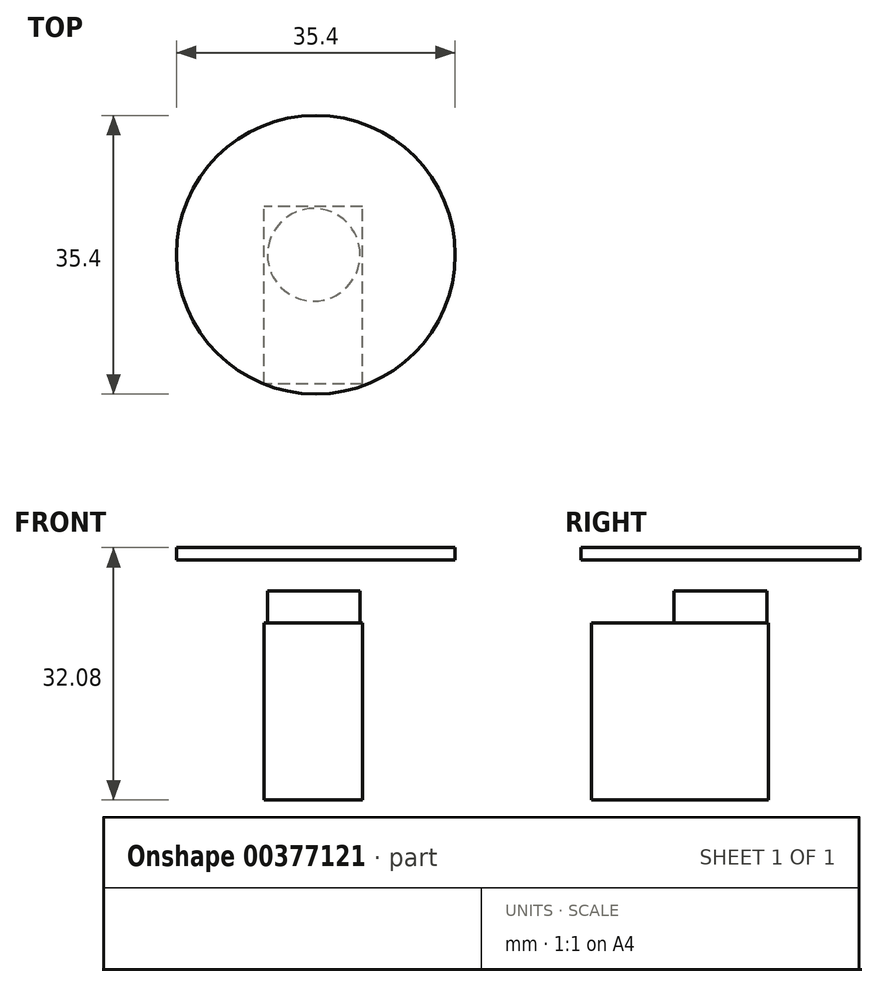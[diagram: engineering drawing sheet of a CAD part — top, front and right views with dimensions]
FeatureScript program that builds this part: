
annotation { "Feature Type Name" : "Feature", "Feature Type Description" : "" }
export const myFeature = defineFeature(function(context is Context, id is Id, definition is map)
    precondition{}
    {
        {
            var Q0;
            Q0=qCreatedBy(makeId("Right.planeOp"),FACE);
            var sketch = newSketch(context, id + "F0", { "sketchPlane" : qUnion([Q0])});
            skLineSegment(sketch, "E0.bottom", {"start": v(0, 0) * mm, "end": v(22.5, 0) * mm});
            skLineSegment(sketch, "E0.top", {"start": v(0, 22.5) * mm, "end": v(22.5, 22.5) * mm});
            skLineSegment(sketch, "E0.left", {"start": v(0, 0) * mm, "end": v(0, 22.5) * mm});
            skLineSegment(sketch, "E0.right", {"start": v(22.5, 0) * mm, "end": v(22.5, 22.5) * mm});
            skSolve(sketch);
        }
        {
            var Q0;
            Q0=makeQuery(id+"F0.imprint","IMPRINT",FACE,{"disambiguationData":[TD([[makeQuery(id+"F0.imprint","IMPRINT",EDGE,{"derivedFrom":sQuery(id+"F0.wireOp",EDGE,"E0.bottom")}),1.0]])]});
            extrude(context, id + "F1", {"entities" : qUnion([Q0]), "depth" : 12.5 * mm});
        }
        {
            var Q0;
            Q0=qCreatedBy(makeId("Top.planeOp"),FACE);
            var sketch = newSketch(context, id + "F2", { "sketchPlane" : qUnion([Q0])});
            skLineSegment(sketch, "E1", {"start": v(0, 0) * mm, "end": v(0, 12.4) * mm});
            skCircle(sketch, "E2", {"center": v(6.33, 16.4) * mm, "radius": 5.88 * mm});
            skSolve(sketch);
        }
        {
            var Q0;
            Q0 = qSketchRegion(id + "F2", true);
            extrude(context, id + "F3", {"entities" : qUnion([Q0]), "operationType" : NewBodyOperationType.ADD, "depth" : 26.6 * mm});
        }
        {
            var Q0;
            Q0=qCreatedBy(makeId("Top.planeOp"),FACE);
            var sketch = newSketch(context, id + "F4", { "sketchPlane" : qUnion([Q0])});
            skCircle(sketch, "E3", {"center": v(6.33, 16.55) * mm, "radius": 2.9 * mm});
            skSolve(sketch);
        }
        {
            var Q0;
            Q0=sQuery(id+"F4.wireOp",EDGE,"E3");
            extrude(context, id + "F5", {"bodyType" : ToolBodyType.SURFACE, "surfaceEntities" : qUnion([Q0]), "depth" : 30.2 * mm});
        }
        {
            var Q0;
            Q0=qCreatedBy(makeId("Top.planeOp"),FACE);
            var sketch = newSketch(context, id + "F6", { "sketchPlane" : qUnion([Q0])});
            skCircle(sketch, "E4", {"center": v(61.96, -52.93) * mm, "radius": 17.7 * mm});
            skSolve(sketch);
        }
        {
            var Q0;
            Q0=makeQuery(id+"F6.imprint","IMPRINT",FACE,{"disambiguationData":[TD([[makeQuery(id+"F6.imprint","IMPRINT",EDGE,{"derivedFrom":sQuery(id+"F6.wireOp",EDGE,"E4")}),1.0]])]});
            extrude(context, id + "F7", {"entities" : qUnion([Q0]), "depth" : 1.6 * mm});
        }
        {
            var Q0;
            Q0=makeQuery(id+"F7.opExtrude","SWEPT_BODY",BODY,{"disambiguationData":[OSD([sQuery(id+"F6.wireOp",EDGE,"E4")])]});
            transform(context, id + "F8", {"entities" : qUnion([Q0]), "transformType" : TransformType.TRANSLATION_3D, "dx" : -55.37 * mm, "dy" : 69.34 * mm, "dz" : 30.48 * mm, "makeCopy" : true});
        }
        {
            var Q0;
            Q0=makeQuery(id+"F7.opExtrude","SWEPT_BODY",BODY,{"disambiguationData":[OSD([sQuery(id+"F6.wireOp",EDGE,"E4")])]});
            deleteBodies(context, id + "F9", {"entities" : qUnion([Q0])});
        }
    });
